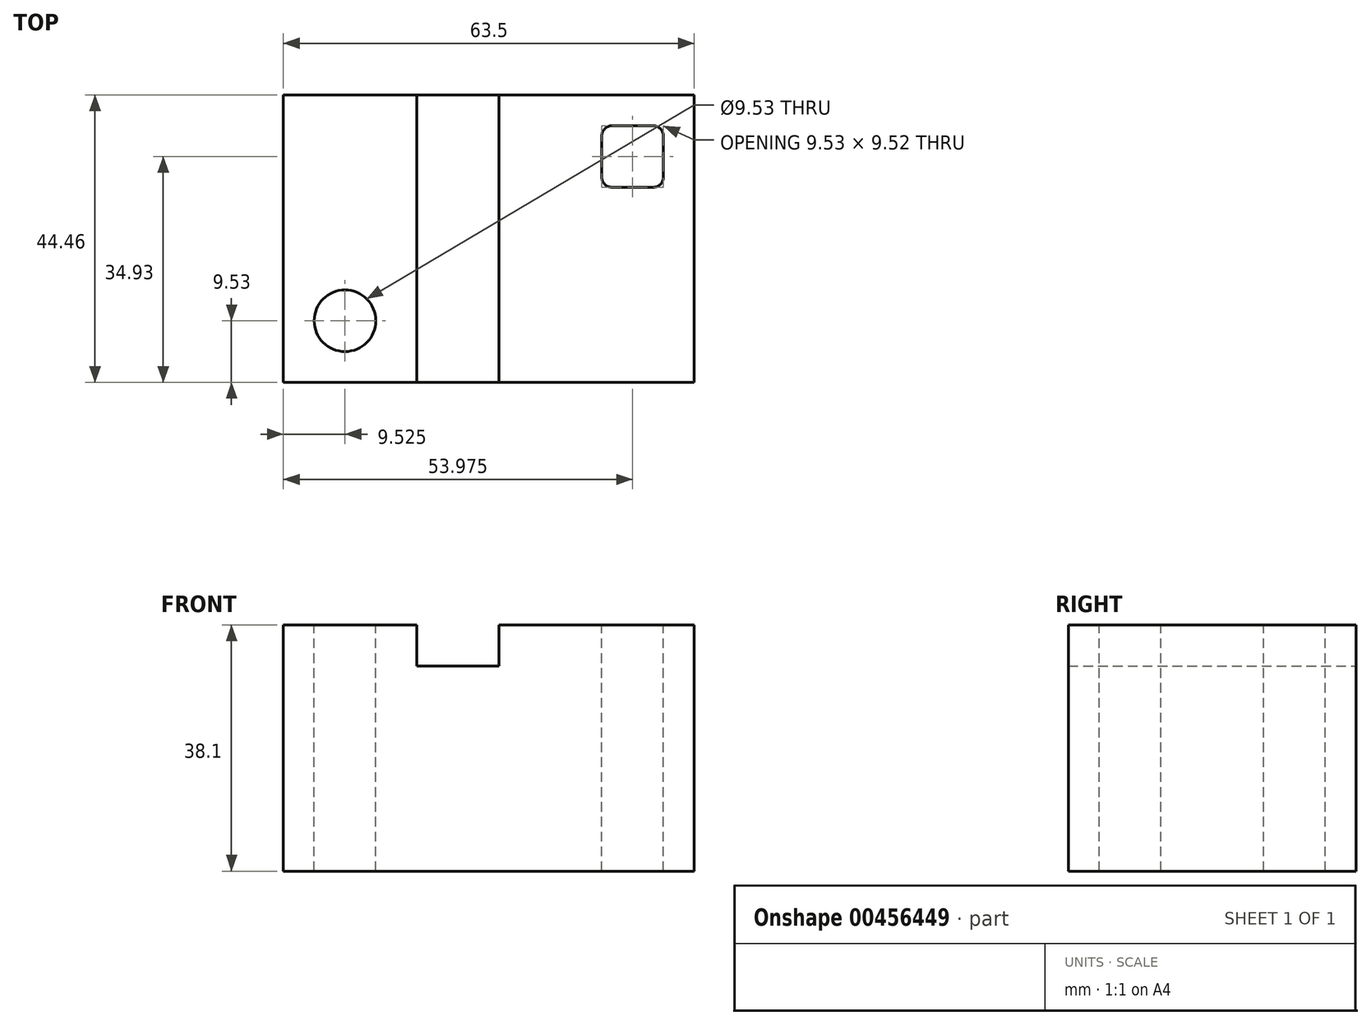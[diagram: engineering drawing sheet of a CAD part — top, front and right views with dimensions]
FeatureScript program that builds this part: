
annotation { "Feature Type Name" : "Feature", "Feature Type Description" : "" }
export const myFeature = defineFeature(function(context is Context, id is Id, definition is map)
    precondition{}
    {
        {
            var Q0;
            Q0=qCreatedBy(makeId("Front.planeOp"),FACE);
            var sketch = newSketch(context, id + "F0", { "sketchPlane" : qUnion([Q0])});
            skLineSegment(sketch, "E0.bottom", {"start": v(31.75, -19.05) * mm, "end": v(-31.75, -19.05) * mm});
            skLineSegment(sketch, "E0.top", {"start": v(31.75, 19.05) * mm, "end": v(1.59, 19.05) * mm});
            skLineSegment(sketch, "E0.left", {"start": v(31.75, -19.05) * mm, "end": v(31.75, 19.05) * mm});
            skLineSegment(sketch, "E0.right", {"start": v(-31.75, -19.05) * mm, "end": v(-31.75, 19.05) * mm});
            skPoint(sketch, "E0.middle", {"position": v(0, 0) * mm});
            skLineSegment(sketch, "E1.top", {"start": v(-11.11, 12.7) * mm, "end": v(1.59, 12.7) * mm});
            skLineSegment(sketch, "E1.left", {"start": v(-11.11, 19.05) * mm, "end": v(-11.11, 12.7) * mm});
            skLineSegment(sketch, "E1.right", {"start": v(1.59, 19.05) * mm, "end": v(1.59, 12.7) * mm});
            skLineSegment(sketch, "E2.trimOffspring", {"start": v(-11.11, 19.05) * mm, "end": v(-31.75, 19.05) * mm});
            skSolve(sketch);
        }
        {
            var Q0;
            Q0 = qSketchRegion(id + "F0", true);
            extrude(context, id + "F1", {"entities" : qUnion([Q0]), "endBound" : BoundingType.SYMMETRIC, "depth" : 44.45 * mm});
        }
        {
            var Q0;
            Q0=makeQuery(id+"F1.opExtrude","SWEPT_FACE",FACE,{"disambiguationData":[OSD([sQuery(id+"F0.wireOp",EDGE,"E2.trimOffspring")])]});
            var sketch = newSketch(context, id + "F2", { "sketchPlane" : qUnion([Q0])});
            skLineSegment(sketch, "E3", {"start": v(-22.23, -22.23) * mm, "end": v(-22.23, -7.94) * mm});
            skLineSegment(sketch, "E4", {"start": v(-31.75, -12.7) * mm, "end": v(-17.46, -12.7) * mm});
            skPoint(sketch, "E5", {"position": v(-22.23, -12.7) * mm});
            skCircle(sketch, "E6", {"center": v(-22.23, -12.7) * mm, "radius": 4.76 * mm});
            skLineSegment(sketch, "E7", {"start": v(22.22, 26) * mm, "end": v(22.22, -31.38) * mm});
            skLineSegment(sketch, "E8", {"start": v(40.51, 12.7) * mm, "end": v(-46.9, 12.7) * mm});
            skPoint(sketch, "E9", {"position": v(22.22, 12.7) * mm});
            skLineSegment(sketch, "E10.bottom", {"start": v(26.99, 7.94) * mm, "end": v(17.46, 7.94) * mm});
            skLineSegment(sketch, "E10.top", {"start": v(26.99, 17.46) * mm, "end": v(17.46, 17.46) * mm});
            skLineSegment(sketch, "E10.left", {"start": v(26.99, 7.94) * mm, "end": v(26.99, 17.46) * mm});
            skLineSegment(sketch, "E10.right", {"start": v(17.46, 7.94) * mm, "end": v(17.46, 17.46) * mm});
            skSolve(sketch);
        }
        {
            var Q0;
            Q0 = qSketchRegion(id + "F2", true);
            extrude(context, id + "F3", {"entities" : qUnion([Q0]), "operationType" : NewBodyOperationType.REMOVE, "endBound" : BoundingType.THROUGH_ALL, "oppositeDirection" : true, "depth" : 25.4 * mm});
        }
        {
            var Q0;
            Q0=makeQuery(id+"F3.boolean.opBoolean","COPY",EDGE,{"derivedFrom":makeQuery(id+"F3.opExtrude","SWEPT_EDGE",EDGE,{"disambiguationData":[OSD([sQuery(id+"F2.wireOp",EDGE,"E10.top"),sQuery(id+"F2.wireOp",EDGE,"E10.right")])]})});
            var Q1;
            Q1=makeQuery(id+"F3.boolean.opBoolean","COPY",EDGE,{"derivedFrom":makeQuery(id+"F3.opExtrude","SWEPT_EDGE",EDGE,{"disambiguationData":[OSD([sQuery(id+"F2.wireOp",EDGE,"E10.bottom"),sQuery(id+"F2.wireOp",EDGE,"E10.right")])]})});
            var Q2;
            Q2=makeQuery(id+"F3.boolean.opBoolean","COPY",EDGE,{"derivedFrom":makeQuery(id+"F3.opExtrude","SWEPT_EDGE",EDGE,{"disambiguationData":[OSD([sQuery(id+"F2.wireOp",EDGE,"E10.bottom"),sQuery(id+"F2.wireOp",EDGE,"E10.left")])]})});
            var Q3;
            Q3=makeQuery(id+"F3.boolean.opBoolean","COPY",EDGE,{"derivedFrom":makeQuery(id+"F3.opExtrude","SWEPT_EDGE",EDGE,{"disambiguationData":[OSD([sQuery(id+"F2.wireOp",EDGE,"E10.top"),sQuery(id+"F2.wireOp",EDGE,"E10.left")])]})});
            fillet(context, id + "F4", {"entities" : qUnion([Q0, Q1, Q2, Q3]), "radius" : 1.59 * mm, "tangentPropagation" : true, "allowEdgeOverflow" : false});
        }
    });
